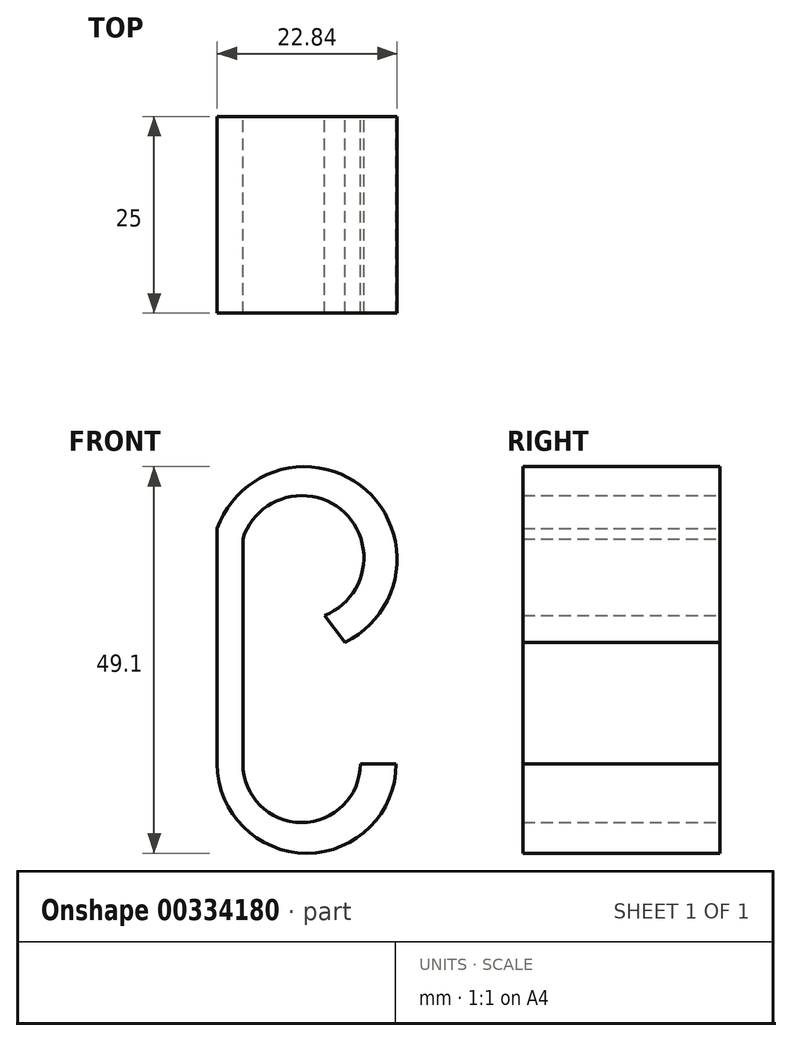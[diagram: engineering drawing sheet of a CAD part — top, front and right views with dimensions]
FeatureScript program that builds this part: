
annotation { "Feature Type Name" : "Feature", "Feature Type Description" : "" }
export const myFeature = defineFeature(function(context is Context, id is Id, definition is map)
    precondition{}
    {
        {
            var Q0;
            Q0=qCreatedBy(makeId("Front.planeOp"),FACE);
            var sketch = newSketch(context, id + "F0", { "sketchPlane" : qUnion([Q0])});
            skLineSegment(sketch, "E0", {"start": v(-30.53, 14.45) * mm, "end": v(-30.53, -15.43) * mm});
            skArc(sketch, "E1", {"start": v(-14.29, 0) * mm, "mid": v(-11.63, 19.34) * mm, "end": v(-30.53, 14.45) * mm});
            skArc(sketch, "E2", {"start": v(-16.89, 3.4) * mm, "mid": v(-14.39, 16.5) * mm, "end": v(-27.28, 13.15) * mm});
            skLineSegment(sketch, "E3", {"start": v(-16.89, 3.4) * mm, "end": v(-14.29, 0) * mm});
            skLineSegment(sketch, "E4", {"start": v(-27.28, 13.15) * mm, "end": v(-27.28, -15.43) * mm});
            skArc(sketch, "E5", {"start": v(-30.53, -15.43) * mm, "mid": v(-19.16, -26.8) * mm, "end": v(-7.8, -15.43) * mm});
            skArc(sketch, "E6", {"start": v(-27.28, -15.43) * mm, "mid": v(-19.8, -22.9) * mm, "end": v(-12.34, -15.43) * mm});
            skLineSegment(sketch, "E7", {"start": v(-12.34, -15.43) * mm, "end": v(-7.8, -15.43) * mm});
            skSolve(sketch);
        }
        {
            var Q0;
            Q0 = qSketchRegion(id + "F0", true);
            extrude(context, id + "F1", {"entities" : qUnion([Q0]), "depth" : 25 * mm});
        }
    });
